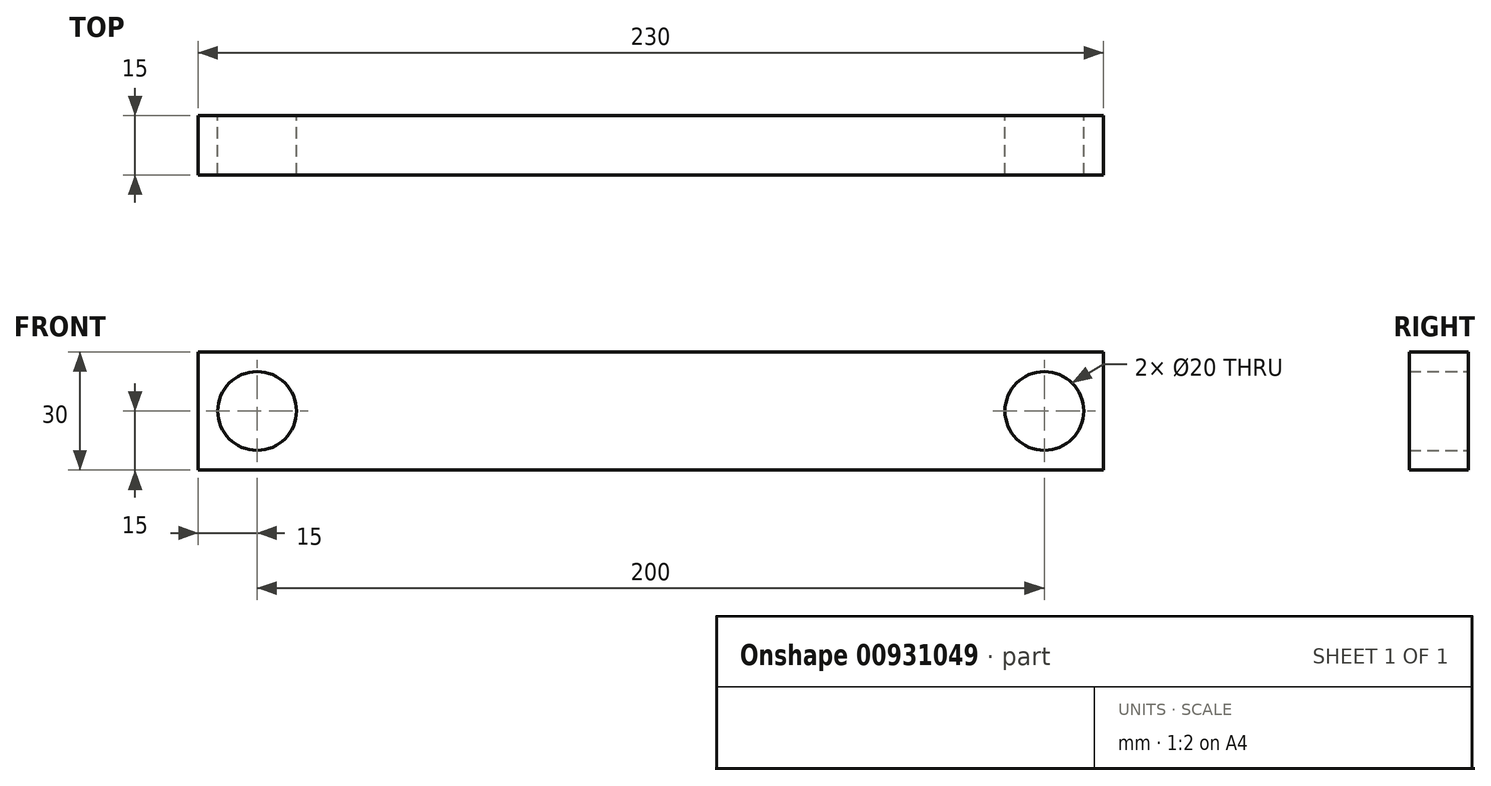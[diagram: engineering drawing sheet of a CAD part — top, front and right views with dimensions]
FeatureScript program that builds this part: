
annotation { "Feature Type Name" : "Feature", "Feature Type Description" : "" }
export const myFeature = defineFeature(function(context is Context, id is Id, definition is map)
    precondition{}
    {
        {
            var Q0;
            Q0=qCreatedBy(makeId("Front.planeOp"),FACE);
            var sketch = newSketch(context, id + "F0", { "sketchPlane" : qUnion([Q0])});
            skCircle(sketch, "E0", {"center": v(0, 0) * mm, "radius": 10 * mm});
            skCircle(sketch, "E1", {"center": v(-200, 0) * mm, "radius": 10 * mm});
            skLineSegment(sketch, "E2.bottom", {"start": v(15, 15) * mm, "end": v(-215, 15) * mm});
            skLineSegment(sketch, "E2.top", {"start": v(15, -15) * mm, "end": v(-215, -15) * mm});
            skLineSegment(sketch, "E2.left", {"start": v(15, 15) * mm, "end": v(15, -15) * mm});
            skLineSegment(sketch, "E2.right", {"start": v(-215, 15) * mm, "end": v(-215, -15) * mm});
            skPoint(sketch, "E2.middle", {"position": v(-100, 0) * mm});
            skSolve(sketch);
        }
        {
            var Q0;
            Q0=makeQuery(id+"F0.imprint","IMPRINT",FACE,{"disambiguationData":[TD([[makeQuery(id+"F0.imprint","IMPRINT",EDGE,{"derivedFrom":sQuery(id+"F0.wireOp",EDGE,"E0")}),-1.0]])]});
            extrude(context, id + "F1", {"entities" : qUnion([Q0]), "depth" : 15 * mm, "offsetDistance" : 25 * mm, "symmetric" : true});
        }
    });
